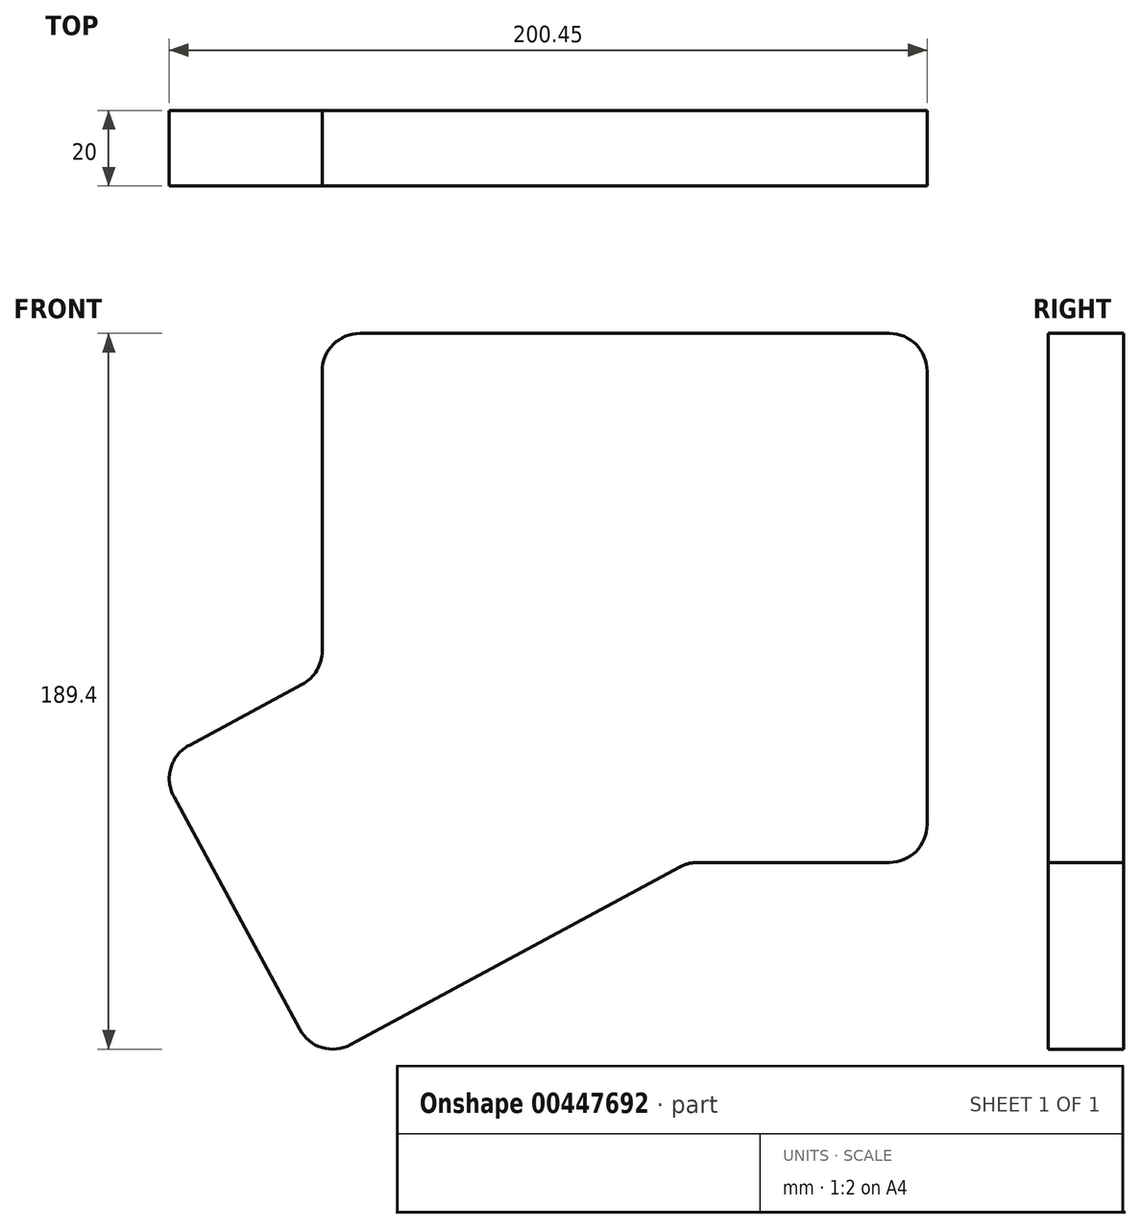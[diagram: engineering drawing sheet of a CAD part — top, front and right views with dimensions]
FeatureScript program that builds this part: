
annotation { "Feature Type Name" : "Feature", "Feature Type Description" : "" }
export const myFeature = defineFeature(function(context is Context, id is Id, definition is map)
    precondition{}
    {
        {
            var Q0;
            Q0=qCreatedBy(makeId("Front.planeOp"),FACE);
            var sketch = newSketch(context, id + "F0", { "sketchPlane" : qUnion([Q0])});
            skLineSegment(sketch, "E0.bottom", {"start": v(10, 90) * mm, "end": v(150, 90) * mm});
            skLineSegment(sketch, "E0.top", {"start": v(99.37, -50) * mm, "end": v(150, -50) * mm});
            skLineSegment(sketch, "E0.left", {"start": v(0, 80) * mm, "end": v(0, 5.97) * mm});
            skLineSegment(sketch, "E0.right", {"start": v(160, 80) * mm, "end": v(160, -40) * mm});
            skLineSegment(sketch, "E1", {"start": v(-5.25, -2.83) * mm, "end": v(-35.2, -19) * mm});
            skLineSegment(sketch, "E2", {"start": v(-39.25, -32.55) * mm, "end": v(-6, -94.15) * mm});
            skLineSegment(sketch, "E3", {"start": v(7.55, -98.2) * mm, "end": v(94.62, -51.2) * mm});
            skPoint(sketch, "E4.visualSharp", {"position": v(0, 90) * mm});
            skArc(sketch, "E4.filletArc", {"start": v(10, 90) * mm, "mid": v(2.93, 87.07) * mm, "end": v(0, 80) * mm});
            skPoint(sketch, "E5.visualSharp", {"position": v(160, 90) * mm});
            skArc(sketch, "E5.filletArc", {"start": v(160, 80) * mm, "mid": v(157.07, 87.07) * mm, "end": v(150, 90) * mm});
            skPoint(sketch, "E6.visualSharp", {"position": v(160, -50) * mm});
            skArc(sketch, "E6.filletArc", {"start": v(150, -50) * mm, "mid": v(157.07, -47.07) * mm, "end": v(160, -40) * mm});
            skPoint(sketch, "E7.visualSharp", {"position": v(96.85, -50) * mm});
            skArc(sketch, "E7.filletArc", {"start": v(99.37, -50) * mm, "mid": v(96.92, -50.3) * mm, "end": v(94.62, -51.2) * mm});
            skPoint(sketch, "E8.visualSharp", {"position": v(-1.25, -102.95) * mm});
            skArc(sketch, "E8.filletArc", {"start": v(-6, -94.15) * mm, "mid": v(-0.07, -98.98) * mm, "end": v(7.55, -98.2) * mm});
            skPoint(sketch, "E9.visualSharp", {"position": v(0, 0) * mm});
            skArc(sketch, "E9.filletArc", {"start": v(-5.25, -2.83) * mm, "mid": v(-1.41, 0.84) * mm, "end": v(0, 5.97) * mm});
            skPoint(sketch, "E10.visualSharp", {"position": v(-44, -23.75) * mm});
            skArc(sketch, "E10.filletArc", {"start": v(-35.2, -19) * mm, "mid": v(-40.03, -24.93) * mm, "end": v(-39.25, -32.55) * mm});
            skSolve(sketch);
        }
        {
            var Q0;
            Q0 = qSketchRegion(id + "F0", true);
            extrude(context, id + "F1", {"entities" : qUnion([Q0]), "depth" : 20 * mm});
        }
    });
